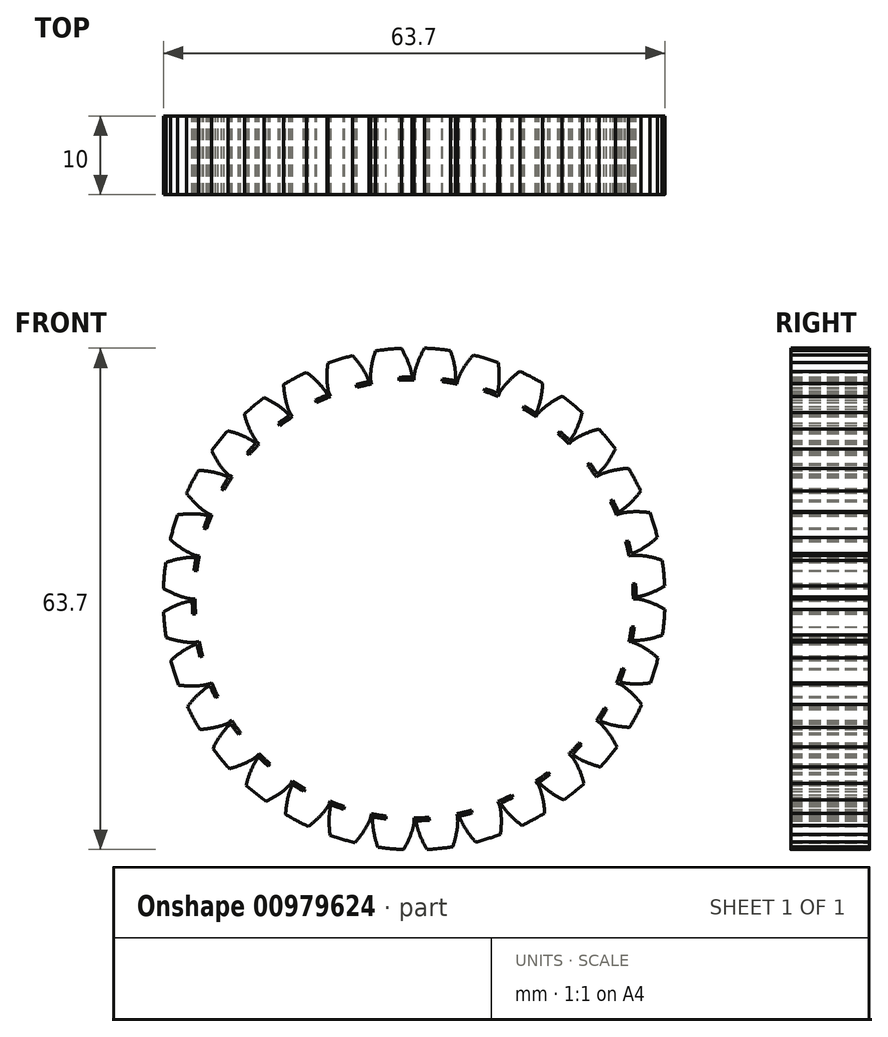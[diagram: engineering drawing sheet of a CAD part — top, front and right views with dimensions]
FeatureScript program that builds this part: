
annotation { "Feature Type Name" : "Feature", "Feature Type Description" : "" }
export const myFeature = defineFeature(function(context is Context, id is Id, definition is map)
    precondition{}
    {
        {
            assignVariable(context, id + "F0", {"name" : "ToothCount", "anyValue" : 32});
        }
        {
            var Q0;
            Q0=qCreatedBy(makeId("Front.planeOp"),FACE);
            var sketch = newSketch(context, id + "F1", { "sketchPlane" : qUnion([Q0])});
            skCircle(sketch, "E0", {"center": v(0, 0) * mm, "radius": 30 * mm});
            skCircle(sketch, "E1", {"center": v(0, 0) * mm, "radius": 28.2 * mm});
            skCircle(sketch, "E2", {"center": v(0, 0) * mm, "radius": 27.83 * mm});
            skCircle(sketch, "E3", {"center": v(0, 0) * mm, "radius": 31.88 * mm});
            skLineSegment(sketch, "E4", {"start": v(0, 0) * mm, "end": v(0, 28.2) * mm});
            skLineSegment(sketch, "E5.1.0", {"start": v(0, 0) * mm, "end": v(1.4, 28.16) * mm});
            skLineSegment(sketch, "E5.2.0", {"start": v(0, 0) * mm, "end": v(2.81, 28.05) * mm});
            skLineSegment(sketch, "E5.3.0", {"start": v(0, 0) * mm, "end": v(4.21, 27.87) * mm});
            skLineSegment(sketch, "E5.4.0", {"start": v(0, 0) * mm, "end": v(5.6, 27.63) * mm});
            skLineSegment(sketch, "E5.5.0", {"start": v(0, 0) * mm, "end": v(6.97, 27.31) * mm});
            skLineSegment(sketch, "E5.6.0", {"start": v(0, 0) * mm, "end": v(8.33, 26.93) * mm});
            skLineSegment(sketch, "E5.7.0", {"start": v(0, 0) * mm, "end": v(9.67, 26.48) * mm});
            skLineSegment(sketch, "E5.8.0", {"start": v(0, 0) * mm, "end": v(10.98, 25.97) * mm});
            skLineSegment(sketch, "E5.9.0", {"start": v(0, 0) * mm, "end": v(12.26, 25.38) * mm});
            skLineSegment(sketch, "E5.10.0", {"start": v(0, 0) * mm, "end": v(13.52, 24.74) * mm});
            skLineSegment(sketch, "E5.11.0", {"start": v(0, 0) * mm, "end": v(14.73, 24.03) * mm});
            skLineSegment(sketch, "E5.12.0", {"start": v(0, 0) * mm, "end": v(15.92, 23.27) * mm});
            skLineSegment(sketch, "E5.13.0", {"start": v(0, 0) * mm, "end": v(17.06, 22.44) * mm});
            skLineSegment(sketch, "E5.14.0", {"start": v(0, 0) * mm, "end": v(18.16, 21.56) * mm});
            skLineSegment(sketch, "E5.15.0", {"start": v(0, 0) * mm, "end": v(19.22, 20.63) * mm});
            skLineSegment(sketch, "E5.16.0", {"start": v(0, 0) * mm, "end": v(20.22, 19.64) * mm});
            skLineSegment(sketch, "E5.17.0", {"start": v(0, 0) * mm, "end": v(21.18, 18.6) * mm});
            skLineSegment(sketch, "E5.18.0", {"start": v(0, 0) * mm, "end": v(22.08, 17.52) * mm});
            skLineSegment(sketch, "E5.19.0", {"start": v(0, 0) * mm, "end": v(22.93, 16.4) * mm});
            skLineSegment(sketch, "E5.anchor1", {"start": v(0, 0) * mm, "end": v(0, 28.2) * mm, "construction": true});
            skLineSegment(sketch, "E5.anchor2", {"start": v(0, 0) * mm, "end": v(22.93, 16.4) * mm, "construction": true});
            skLineSegment(sketch, "E6", {"start": v(1.4, 28.16) * mm, "end": v(0, 28.23) * mm});
            skLineSegment(sketch, "E7", {"start": v(2.81, 28.05) * mm, "end": v(0, 28.33) * mm});
            skLineSegment(sketch, "E8", {"start": v(4.21, 27.87) * mm, "end": v(0.03, 28.5) * mm});
            skLineSegment(sketch, "E9", {"start": v(5.6, 27.63) * mm, "end": v(0.07, 28.75) * mm});
            skLineSegment(sketch, "E10", {"start": v(6.97, 27.31) * mm, "end": v(0.15, 29.06) * mm});
            skLineSegment(sketch, "E11", {"start": v(8.33, 26.93) * mm, "end": v(0.25, 29.43) * mm});
            skLineSegment(sketch, "E12", {"start": v(9.67, 26.48) * mm, "end": v(0.4, 29.86) * mm});
            skLineSegment(sketch, "E13", {"start": v(10.98, 25.97) * mm, "end": v(0.6, 30.36) * mm});
            skLineSegment(sketch, "E14", {"start": v(12.26, 25.38) * mm, "end": v(0.84, 30.9) * mm});
            skLineSegment(sketch, "E15", {"start": v(13.52, 24.74) * mm, "end": v(1.15, 31.5) * mm});
            skLineSegment(sketch, "E16", {"start": v(14.73, 24.03) * mm, "end": v(1.52, 32.14) * mm});
            skLineSegment(sketch, "E17", {"start": v(15.92, 23.27) * mm, "end": v(1.96, 32.82) * mm});
            skLineSegment(sketch, "E18", {"start": v(17.06, 22.44) * mm, "end": v(2.47, 33.53) * mm});
            skLineSegment(sketch, "E19", {"start": v(18.16, 21.56) * mm, "end": v(3.07, 34.27) * mm});
            skLineSegment(sketch, "E20", {"start": v(19.22, 20.63) * mm, "end": v(3.75, 35.04) * mm});
            skLineSegment(sketch, "E21", {"start": v(20.22, 19.64) * mm, "end": v(4.51, 35.82) * mm});
            skLineSegment(sketch, "E22", {"start": v(21.18, 18.6) * mm, "end": v(5.36, 36.6) * mm});
            skLineSegment(sketch, "E23", {"start": v(22.08, 17.52) * mm, "end": v(6.31, 37.4) * mm});
            skLineSegment(sketch, "E24", {"start": v(22.93, 16.4) * mm, "end": v(7.35, 38.18) * mm});
            skFitSpline(sketch, "E25", {"points": [v(0, 28.2) * mm, v(0, 28.33) * mm, v(0.03, 28.5) * mm, v(0.07, 28.75) * mm, v(0.15, 29.06) * mm, v(0.25, 29.43) * mm, v(0.4, 29.86) * mm, v(0.6, 30.36) * mm, v(0.84, 30.9) * mm, v(1.15, 31.5) * mm, v(1.52, 32.14) * mm, v(1.96, 32.82) * mm, v(2.47, 33.53) * mm, v(3.07, 34.27) * mm, v(3.75, 35.04) * mm, v(4.51, 35.82) * mm, v(5.36, 36.6) * mm, v(6.31, 37.4) * mm, v(7.35, 38.18) * mm], "startDerivative": vector(0.28, 5.34) * mm, "endDerivative": vector(13.44, 9.9) * mm});
            skSolve(sketch);
        }
        {
            var Q0;
            Q0=qCreatedBy(makeId("Front.planeOp"),FACE);
            var sketch = newSketch(context, id + "F2", { "sketchPlane" : qUnion([Q0])});
            skCircle(sketch, "E26.0", {"center": v(0, 0) * mm, "radius": 27.83 * mm});
            skCircle(sketch, "E27.0", {"center": v(0, 0) * mm, "radius": 28.2 * mm});
            skCircle(sketch, "E28.0", {"center": v(0, 0) * mm, "radius": 30 * mm});
            skCircle(sketch, "E29.0", {"center": v(0, 0) * mm, "radius": 31.88 * mm});
            skFitSpline(sketch, "E30.0", {"points": [v(0, 28.2) * mm, v(0, 28.24) * mm, v(0, 28.33) * mm, v(0.03, 28.51) * mm, v(0.07, 28.76) * mm, v(0.14, 29.06) * mm, v(0.25, 29.44) * mm, v(0.4, 29.87) * mm, v(0.59, 30.36) * mm, v(0.84, 30.9) * mm, v(1.14, 31.5) * mm, v(1.51, 32.15) * mm, v(1.96, 32.83) * mm, v(2.47, 33.54) * mm, v(3.07, 34.28) * mm, v(3.74, 35.05) * mm, v(4.5, 35.83) * mm, v(5.36, 36.62) * mm, v(6.3, 37.41) * mm, v(7, 37.92) * mm, v(7.35, 38.18) * mm]});
            skPoint(sketch, "E31.orphan", {"position": v(7.35, 38.18) * mm});
            skLineSegment(sketch, "E32", {"start": v(0, 0) * mm, "end": v(0.45, 30) * mm});
            skLineSegment(sketch, "E33", {"start": v(0, 0) * mm, "end": v(1.92, 29.94) * mm});
            skLineSegment(sketch, "E34", {"start": v(0, 28.2) * mm, "end": v(0, 0) * mm});
            skFitSpline(sketch, "E35.MirrorCS", {"points": [v(5.24, 27.7) * mm, v(5.24, 27.75) * mm, v(5.26, 27.84) * mm, v(5.27, 28.02) * mm, v(5.27, 28.27) * mm, v(5.26, 28.59) * mm, v(5.22, 28.97) * mm, v(5.16, 29.43) * mm, v(5.06, 29.94) * mm, v(4.92, 30.53) * mm, v(4.73, 31.17) * mm, v(4.48, 31.87) * mm, v(4.18, 32.62) * mm, v(3.8, 33.42) * mm, v(3.36, 34.26) * mm, v(2.83, 35.13) * mm, v(2.23, 36.04) * mm, v(1.53, 36.98) * mm, v(0.75, 37.93) * mm, v(0.17, 38.56) * mm, v(-0.13, 38.88) * mm]});
            skLineSegment(sketch, "E36.MirrorCS", {"start": v(3.6, 27.96) * mm, "end": v(0, 0) * mm});
            skSolve(sketch);
        }
        {
            var Q0;
            {var subQ0=sQuery(id+"F2.wireOp",EDGE,"E36.MirrorCS");var subQ1=sQuery(id+"F2.wireOp",EDGE,"E26.0");var subQ2=makeQuery(id+"F2.imprint","INTERSECT",VERTEX,{"derivedFrom":[subQ1,subQ0]});Q0=makeQuery(id+"F2.imprint","IMPRINT",FACE,{"disambiguationData":[TD([[makeQuery(id+"F2.imprint","IMPRINT",EDGE,{"disambiguationData":[TD([[subQ2,1.0]])],"derivedFrom":subQ1}),1.0]])]});}
            var Q1;
            {var subQ0=sQuery(id+"F2.wireOp",EDGE,"E33");var subQ1=sQuery(id+"F2.wireOp",EDGE,"E26.0");var subQ2=makeQuery(id+"F2.imprint","INTERSECT",VERTEX,{"derivedFrom":[subQ1,subQ0]});Q1=makeQuery(id+"F2.imprint","IMPRINT",FACE,{"disambiguationData":[TD([[makeQuery(id+"F2.imprint","IMPRINT",EDGE,{"disambiguationData":[TD([[subQ2,-1.0]])],"derivedFrom":subQ1}),1.0]])]});}
            var Q2;
            {var subQ0=sQuery(id+"F2.wireOp",EDGE,"E32");var subQ1=sQuery(id+"F2.wireOp",EDGE,"E26.0");var subQ2=makeQuery(id+"F2.imprint","INTERSECT",VERTEX,{"derivedFrom":[subQ1,subQ0]});Q2=makeQuery(id+"F2.imprint","IMPRINT",FACE,{"disambiguationData":[TD([[makeQuery(id+"F2.imprint","IMPRINT",EDGE,{"disambiguationData":[TD([[subQ2,-1.0]])],"derivedFrom":subQ1}),1.0]])]});}
            var Q3;
            {var subQ0=sQuery(id+"F2.wireOp",EDGE,"E33");var subQ1=sQuery(id+"F2.wireOp",EDGE,"E26.0");var subQ2=makeQuery(id+"F2.imprint","INTERSECT",VERTEX,{"derivedFrom":[subQ1,subQ0]});Q3=makeQuery(id+"F2.imprint","IMPRINT",FACE,{"disambiguationData":[TD([[makeQuery(id+"F2.imprint","IMPRINT",EDGE,{"disambiguationData":[TD([[subQ2,1.0]])],"derivedFrom":subQ1}),1.0]])]});}
            var Q4;
            {var subQ0=sQuery(id+"F2.wireOp",EDGE,"E33");var subQ1=sQuery(id+"F2.wireOp",EDGE,"E26.0");var subQ2=makeQuery(id+"F2.imprint","INTERSECT",VERTEX,{"derivedFrom":[subQ1,subQ0]});Q4=makeQuery(id+"F2.imprint","IMPRINT",FACE,{"disambiguationData":[TD([[makeQuery(id+"F2.imprint","IMPRINT",EDGE,{"disambiguationData":[TD([[subQ2,1.0]])],"derivedFrom":subQ1}),-1.0]])]});}
            var Q5;
            {var subQ0=sQuery(id+"F2.wireOp",EDGE,"E32");var subQ1=sQuery(id+"F2.wireOp",EDGE,"E26.0");var subQ2=makeQuery(id+"F2.imprint","INTERSECT",VERTEX,{"derivedFrom":[subQ1,subQ0]});Q5=makeQuery(id+"F2.imprint","IMPRINT",FACE,{"disambiguationData":[TD([[makeQuery(id+"F2.imprint","IMPRINT",EDGE,{"disambiguationData":[TD([[subQ2,-1.0]])],"derivedFrom":subQ1}),-1.0]])]});}
            var Q6;
            {var subQ1=sQuery(id+"F2.wireOp",EDGE,"E27.0");var subQ3=sQuery(id+"F2.wireOp",EDGE,"E32");var subQ4=makeQuery(id+"F2.imprint","INTERSECT",VERTEX,{"derivedFrom":[subQ1,subQ3]});Q6=makeQuery(id+"F2.imprint","IMPRINT",FACE,{"disambiguationData":[TD([[makeQuery(id+"F2.imprint","IMPRINT",EDGE,{"disambiguationData":[TD([[subQ4,-1.0]])],"derivedFrom":subQ1}),-1.0]])]});}
            var Q7;
            {var subQ0=sQuery(id+"F2.wireOp",EDGE,"E33");var subQ1=sQuery(id+"F2.wireOp",EDGE,"E26.0");var subQ2=makeQuery(id+"F2.imprint","INTERSECT",VERTEX,{"derivedFrom":[subQ1,subQ0]});Q7=makeQuery(id+"F2.imprint","IMPRINT",FACE,{"disambiguationData":[TD([[makeQuery(id+"F2.imprint","IMPRINT",EDGE,{"disambiguationData":[TD([[subQ2,-1.0]])],"derivedFrom":subQ1}),-1.0]])]});}
            var Q8;
            {var subQ0=sQuery(id+"F2.wireOp",EDGE,"E33");var subQ1=sQuery(id+"F2.wireOp",EDGE,"E27.0");var subQ2=makeQuery(id+"F2.imprint","INTERSECT",VERTEX,{"derivedFrom":[subQ1,subQ0]});Q8=makeQuery(id+"F2.imprint","IMPRINT",FACE,{"disambiguationData":[TD([[makeQuery(id+"F2.imprint","IMPRINT",EDGE,{"disambiguationData":[TD([[subQ2,-1.0]])],"derivedFrom":subQ1}),-1.0]])]});}
            var Q9;
            {var subQ3=sQuery(id+"F2.wireOp",EDGE,"E33");var subQ5=sQuery(id+"F2.wireOp",EDGE,"E28.0");var subQ6=makeQuery(id+"F2.imprint","INTERSECT",VERTEX,{"derivedFrom":[subQ5,subQ3]});Q9=makeQuery(id+"F2.imprint","IMPRINT",FACE,{"disambiguationData":[TD([[makeQuery(id+"F2.imprint","IMPRINT",EDGE,{"disambiguationData":[TD([[subQ6,1.0]])],"derivedFrom":subQ5}),1.0]])]});}
            var Q10;
            {var subQ5=sQuery(id+"F2.wireOp",EDGE,"E28.0");var subQ7=makeQuery(id+"F2.imprint","INTERSECT",VERTEX,{"derivedFrom":[subQ5,sQuery(id+"F2.wireOp",EDGE,"E33")]});Q10=makeQuery(id+"F2.imprint","IMPRINT",FACE,{"disambiguationData":[TD([[makeQuery(id+"F2.imprint","IMPRINT",EDGE,{"disambiguationData":[TD([[subQ7,1.0]])],"derivedFrom":subQ5}),-1.0]])]});}
            extrude(context, id + "F3", {"entities" : qUnion([Q0, Q1, Q2, Q3, Q4, Q5, Q6, Q7, Q8, Q9, Q10]), "depth" : 10 * mm, "offsetDistance" : 25 * mm});
        }
        {
            var Q0;
            Q0=makeQuery(id+"F3.opExtrude","SWEPT_BODY",BODY,{"disambiguationData":[OSD([sQuery(id+"F2.wireOp",EDGE,"E26.0"),sQuery(id+"F2.wireOp",EDGE,"E29.0"),sQuery(id+"F2.wireOp",EDGE,"E30.0"),sQuery(id+"F2.wireOp",EDGE,"E34"),sQuery(id+"F2.wireOp",EDGE,"E35.MirrorCS"),sQuery(id+"F2.wireOp",EDGE,"E36.MirrorCS")])]});
            var Q1;
            Q1=makeQuery(id+"F3.opExtrude","SWEPT_FACE",FACE,{"disambiguationData":[OSD([sQuery(id+"F2.wireOp",EDGE,"E26.0")])]});
            circularPattern(context, id + "F4", {"operationType" : NewBodyOperationType.ADD, "entities" : qUnion([Q0]), "axis" : qUnion([Q1]), "angle" : 360 * degree, "instanceCount" : getVariable(context, 'ToothCount'), "equalSpace" : true});
        }
    });
